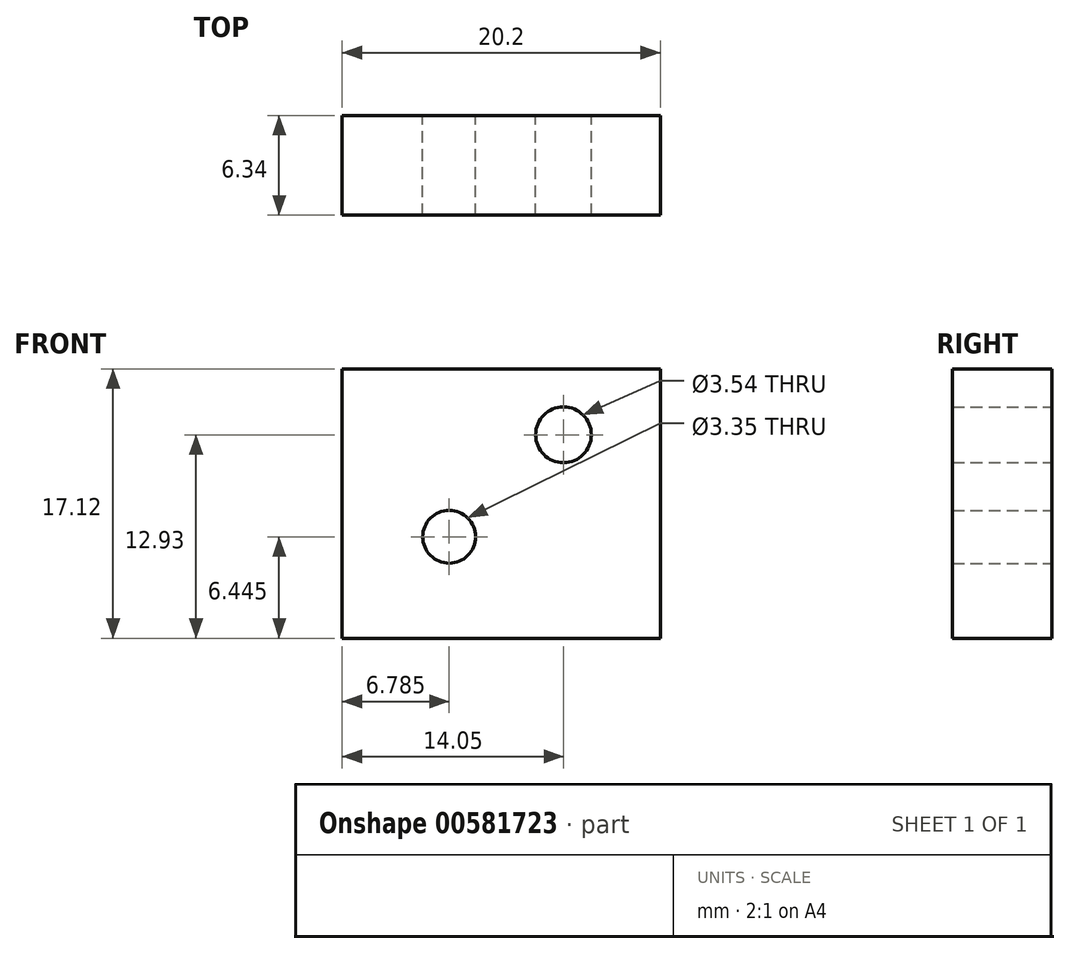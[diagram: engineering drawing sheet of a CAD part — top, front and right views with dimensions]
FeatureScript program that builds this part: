
annotation { "Feature Type Name" : "Feature", "Feature Type Description" : "" }
export const myFeature = defineFeature(function(context is Context, id is Id, definition is map)
    precondition{}
    {
        {
            var Q0;
            Q0=qCreatedBy(makeId("Front.planeOp"),FACE);
            var sketch = newSketch(context, id + "F0", { "sketchPlane" : qUnion([Q0])});
            skLineSegment(sketch, "E0.bottom", {"start": v(-10.1, 8.56) * mm, "end": v(10.1, 8.56) * mm});
            skLineSegment(sketch, "E0.top", {"start": v(-10.1, -8.56) * mm, "end": v(10.1, -8.56) * mm});
            skLineSegment(sketch, "E0.left", {"start": v(-10.1, 8.56) * mm, "end": v(-10.1, -8.56) * mm});
            skLineSegment(sketch, "E0.right", {"start": v(10.1, 8.56) * mm, "end": v(10.1, -8.56) * mm});
            skPoint(sketch, "E0.middle", {"position": v(0, 0) * mm});
            skCircle(sketch, "E1", {"center": v(3.95, 4.37) * mm, "radius": 1.77 * mm});
            skCircle(sketch, "E2", {"center": v(-3.31, -2.11) * mm, "radius": 1.68 * mm});
            skSolve(sketch);
        }
        {
            var Q0;
            Q0=makeQuery(id+"F0.imprint","IMPRINT",FACE,{"disambiguationData":[TD([[makeQuery(id+"F0.imprint","IMPRINT",EDGE,{"derivedFrom":sQuery(id+"F0.wireOp",EDGE,"E0.bottom")}),-1.0]])]});
            extrude(context, id + "F1", {"entities" : qUnion([Q0]), "endBound" : BoundingType.SYMMETRIC, "depth" : 6.33 * mm, "offsetDistance" : 25 * mm});
        }
    });
